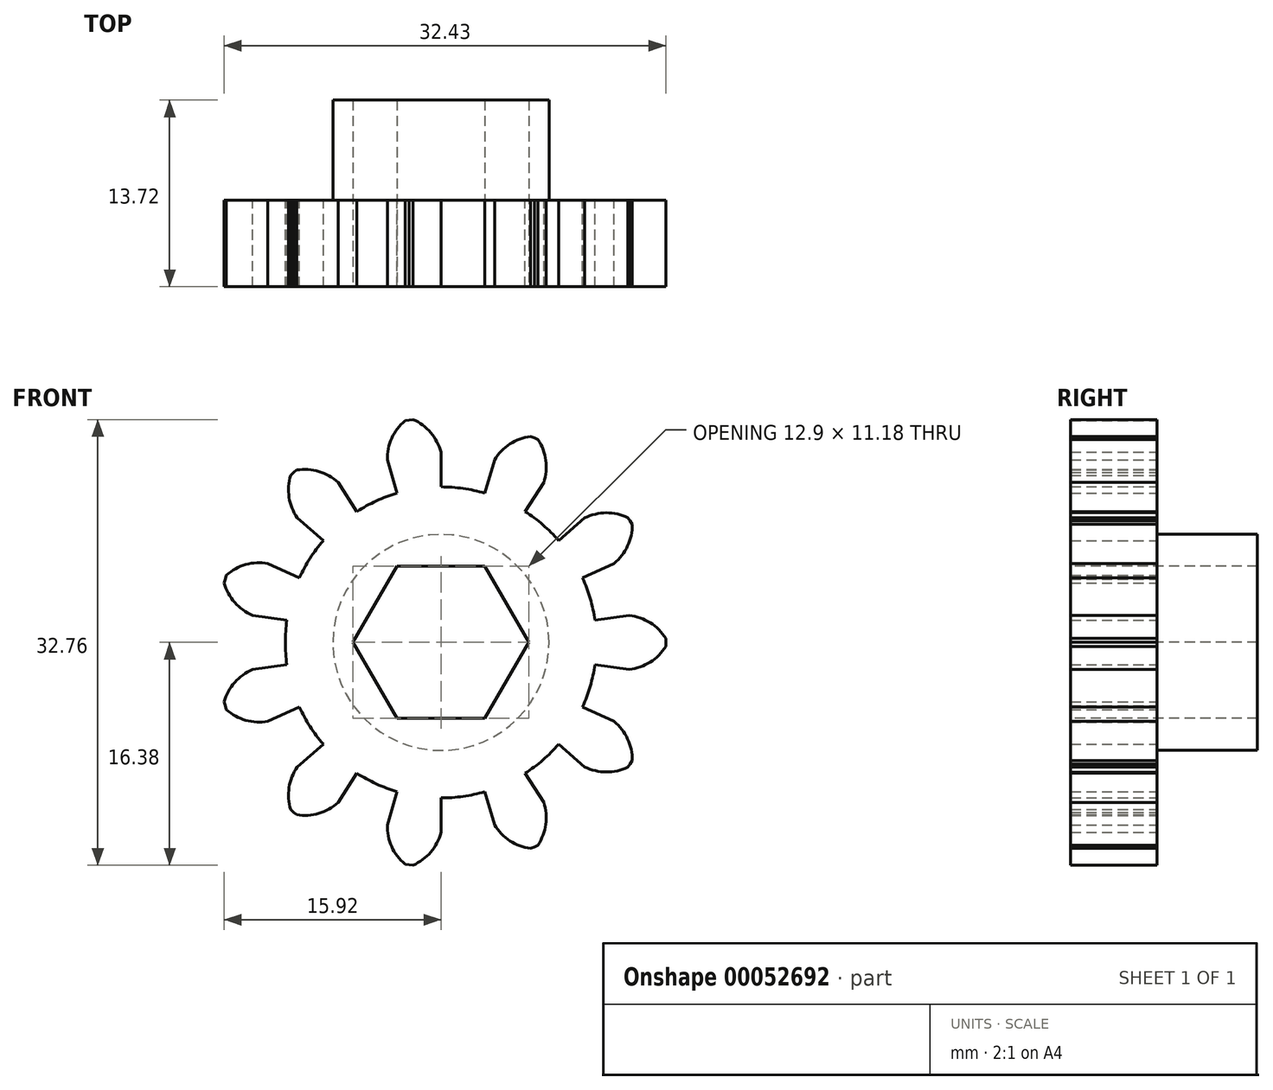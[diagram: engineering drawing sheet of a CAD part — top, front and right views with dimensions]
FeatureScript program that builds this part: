
annotation { "Feature Type Name" : "Feature", "Feature Type Description" : "" }
export const myFeature = defineFeature(function(context is Context, id is Id, definition is map)
    precondition{}
    {
        {
            var Q0;
            Q0=qCreatedBy(makeId("Front.planeOp"),FACE);
            var sketch = newSketch(context, id + "F0", { "sketchPlane" : qUnion([Q0])});
            skArc(sketch, "E0", {"start": v(-3.22, 10.97) * mm, "mid": v(-4.75, 10.4) * mm, "end": v(-6.18, 9.62) * mm});
            skArc(sketch, "E1", {"start": v(0, 13.97) * mm, "mid": v(-0.75, 15.41) * mm, "end": v(-2.06, 16.38) * mm});
            skLineSegment(sketch, "E2", {"start": v(0, 11.43) * mm, "end": v(0, 13.97) * mm});
            skLineSegment(sketch, "E3", {"start": v(-2.06, 16.38) * mm, "end": v(-2.35, 16.34) * mm});
            skLineSegment(sketch, "E4.MirrorCS", {"start": v(-2.64, 16.3) * mm, "end": v(-2.35, 16.34) * mm});
            skArc(sketch, "E5.MirrorCS", {"start": v(-3.93, 13.4) * mm, "mid": v(-3.62, 15) * mm, "end": v(-2.64, 16.3) * mm});
            skLineSegment(sketch, "E6.MirrorCS", {"start": v(-3.22, 10.97) * mm, "end": v(-3.93, 13.4) * mm});
            skLineSegment(sketch, "E7.1.0", {"start": v(-6.18, 9.62) * mm, "end": v(-7.55, 11.75) * mm});
            skArc(sketch, "E7.1.1", {"start": v(-7.55, 11.75) * mm, "mid": v(-8.96, 12.56) * mm, "end": v(-10.59, 12.67) * mm});
            skArc(sketch, "E7.1.2", {"start": v(-10.56, 9.15) * mm, "mid": v(-11.16, 10.66) * mm, "end": v(-11.03, 12.28) * mm});
            skLineSegment(sketch, "E7.1.3", {"start": v(-8.64, 7.49) * mm, "end": v(-10.56, 9.15) * mm});
            skLineSegment(sketch, "E7.1.4", {"start": v(-10.59, 12.67) * mm, "end": v(-10.81, 12.48) * mm});
            skLineSegment(sketch, "E7.1.5", {"start": v(-11.03, 12.28) * mm, "end": v(-10.81, 12.48) * mm});
            skLineSegment(sketch, "E7.2.0", {"start": v(-10.4, 4.75) * mm, "end": v(-12.7, 5.8) * mm});
            skArc(sketch, "E7.2.1", {"start": v(-12.7, 5.8) * mm, "mid": v(-14.33, 5.72) * mm, "end": v(-15.76, 4.93) * mm});
            skArc(sketch, "E7.2.2", {"start": v(-13.83, 1.99) * mm, "mid": v(-15.15, 2.94) * mm, "end": v(-15.92, 4.37) * mm});
            skLineSegment(sketch, "E7.2.3", {"start": v(-11.31, 1.63) * mm, "end": v(-13.83, 1.99) * mm});
            skLineSegment(sketch, "E7.2.4", {"start": v(-15.76, 4.93) * mm, "end": v(-15.84, 4.65) * mm});
            skLineSegment(sketch, "E7.2.5", {"start": v(-15.92, 4.37) * mm, "end": v(-15.84, 4.65) * mm});
            skLineSegment(sketch, "E7.3.0", {"start": v(-11.31, -1.63) * mm, "end": v(-13.83, -1.99) * mm});
            skArc(sketch, "E7.3.1", {"start": v(-13.83, -1.99) * mm, "mid": v(-15.15, -2.94) * mm, "end": v(-15.92, -4.37) * mm});
            skArc(sketch, "E7.3.2", {"start": v(-12.7, -5.8) * mm, "mid": v(-14.33, -5.72) * mm, "end": v(-15.76, -4.93) * mm});
            skLineSegment(sketch, "E7.3.3", {"start": v(-10.4, -4.75) * mm, "end": v(-12.7, -5.8) * mm});
            skLineSegment(sketch, "E7.3.4", {"start": v(-15.92, -4.37) * mm, "end": v(-15.84, -4.65) * mm});
            skLineSegment(sketch, "E7.3.5", {"start": v(-15.76, -4.93) * mm, "end": v(-15.84, -4.65) * mm});
            skLineSegment(sketch, "E7.4.0", {"start": v(-8.64, -7.49) * mm, "end": v(-10.56, -9.15) * mm});
            skArc(sketch, "E7.4.1", {"start": v(-10.56, -9.15) * mm, "mid": v(-11.16, -10.66) * mm, "end": v(-11.03, -12.28) * mm});
            skArc(sketch, "E7.4.2", {"start": v(-7.55, -11.75) * mm, "mid": v(-8.97, -12.56) * mm, "end": v(-10.59, -12.67) * mm});
            skLineSegment(sketch, "E7.4.3", {"start": v(-6.18, -9.62) * mm, "end": v(-7.55, -11.75) * mm});
            skLineSegment(sketch, "E7.4.4", {"start": v(-11.03, -12.28) * mm, "end": v(-10.81, -12.48) * mm});
            skLineSegment(sketch, "E7.4.5", {"start": v(-10.59, -12.67) * mm, "end": v(-10.81, -12.48) * mm});
            skLineSegment(sketch, "E7.5.0", {"start": v(-3.22, -10.97) * mm, "end": v(-3.94, -13.4) * mm});
            skArc(sketch, "E7.5.1", {"start": v(-3.94, -13.4) * mm, "mid": v(-3.62, -15) * mm, "end": v(-2.64, -16.3) * mm});
            skArc(sketch, "E7.5.2", {"start": v(0, -13.97) * mm, "mid": v(-0.75, -15.41) * mm, "end": v(-2.06, -16.38) * mm});
            skLineSegment(sketch, "E7.5.3", {"start": v(0, -11.43) * mm, "end": v(0, -13.97) * mm});
            skLineSegment(sketch, "E7.5.4", {"start": v(-2.64, -16.3) * mm, "end": v(-2.35, -16.34) * mm});
            skLineSegment(sketch, "E7.5.5", {"start": v(-2.06, -16.38) * mm, "end": v(-2.35, -16.34) * mm});
            skLineSegment(sketch, "E7.6.0", {"start": v(3.22, -10.97) * mm, "end": v(3.94, -13.4) * mm});
            skArc(sketch, "E7.6.1", {"start": v(3.94, -13.4) * mm, "mid": v(5.06, -14.58) * mm, "end": v(6.59, -15.14) * mm});
            skArc(sketch, "E7.6.2", {"start": v(7.55, -11.75) * mm, "mid": v(7.7, -13.37) * mm, "end": v(7.12, -14.9) * mm});
            skLineSegment(sketch, "E7.6.3", {"start": v(6.18, -9.62) * mm, "end": v(7.55, -11.75) * mm});
            skLineSegment(sketch, "E7.6.4", {"start": v(6.59, -15.14) * mm, "end": v(6.86, -15.02) * mm});
            skLineSegment(sketch, "E7.6.5", {"start": v(7.12, -14.9) * mm, "end": v(6.86, -15.02) * mm});
            skLineSegment(sketch, "E7.7.0", {"start": v(8.64, -7.49) * mm, "end": v(10.56, -9.15) * mm});
            skArc(sketch, "E7.7.1", {"start": v(10.56, -9.15) * mm, "mid": v(12.14, -9.53) * mm, "end": v(13.73, -9.17) * mm});
            skArc(sketch, "E7.7.2", {"start": v(12.7, -5.8) * mm, "mid": v(13.7, -7.09) * mm, "end": v(14.05, -8.68) * mm});
            skLineSegment(sketch, "E7.7.3", {"start": v(10.4, -4.75) * mm, "end": v(12.7, -5.8) * mm});
            skLineSegment(sketch, "E7.7.4", {"start": v(13.73, -9.17) * mm, "end": v(13.9, -8.93) * mm});
            skLineSegment(sketch, "E7.7.5", {"start": v(14.05, -8.68) * mm, "end": v(13.9, -8.93) * mm});
            skLineSegment(sketch, "E7.8.0", {"start": v(11.31, -1.63) * mm, "end": v(13.83, -1.99) * mm});
            skArc(sketch, "E7.8.1", {"start": v(13.83, -1.99) * mm, "mid": v(15.36, -1.45) * mm, "end": v(16.5, -0.3) * mm});
            skArc(sketch, "E7.8.2", {"start": v(13.83, 1.99) * mm, "mid": v(15.36, 1.45) * mm, "end": v(16.5, 0.3) * mm});
            skLineSegment(sketch, "E7.8.3", {"start": v(11.31, 1.63) * mm, "end": v(13.83, 1.99) * mm});
            skLineSegment(sketch, "E7.8.4", {"start": v(16.5, -0.3) * mm, "end": v(16.51, 0) * mm});
            skLineSegment(sketch, "E7.8.5", {"start": v(16.5, 0.3) * mm, "end": v(16.51, 0) * mm});
            skLineSegment(sketch, "E7.9.0", {"start": v(10.4, 4.75) * mm, "end": v(12.7, 5.8) * mm});
            skArc(sketch, "E7.9.1", {"start": v(12.7, 5.8) * mm, "mid": v(13.7, 7.09) * mm, "end": v(14.05, 8.68) * mm});
            skArc(sketch, "E7.9.2", {"start": v(10.56, 9.15) * mm, "mid": v(12.14, 9.53) * mm, "end": v(13.73, 9.17) * mm});
            skLineSegment(sketch, "E7.9.3", {"start": v(8.64, 7.48) * mm, "end": v(10.56, 9.15) * mm});
            skLineSegment(sketch, "E7.9.4", {"start": v(14.05, 8.68) * mm, "end": v(13.9, 8.93) * mm});
            skLineSegment(sketch, "E7.9.5", {"start": v(13.73, 9.17) * mm, "end": v(13.9, 8.93) * mm});
            skLineSegment(sketch, "E7.10.0", {"start": v(6.18, 9.62) * mm, "end": v(7.55, 11.75) * mm});
            skArc(sketch, "E7.10.1", {"start": v(7.55, 11.75) * mm, "mid": v(7.7, 13.37) * mm, "end": v(7.13, 14.9) * mm});
            skArc(sketch, "E7.10.2", {"start": v(3.94, 13.4) * mm, "mid": v(5.06, 14.58) * mm, "end": v(6.6, 15.14) * mm});
            skLineSegment(sketch, "E7.10.3", {"start": v(3.22, 10.97) * mm, "end": v(3.94, 13.4) * mm});
            skLineSegment(sketch, "E7.10.4", {"start": v(7.13, 14.9) * mm, "end": v(6.86, 15.02) * mm});
            skLineSegment(sketch, "E7.10.5", {"start": v(6.6, 15.14) * mm, "end": v(6.86, 15.02) * mm});
            skArc(sketch, "E8.trimOffspring", {"start": v(-8.64, 7.49) * mm, "mid": v(-9.62, 6.18) * mm, "end": v(-10.4, 4.75) * mm});
            skArc(sketch, "E9.trimOffspring", {"start": v(-11.31, 1.63) * mm, "mid": v(-11.43, 0) * mm, "end": v(-11.31, -1.63) * mm});
            skArc(sketch, "E10.trimOffspring", {"start": v(-10.4, -4.75) * mm, "mid": v(-9.62, -6.18) * mm, "end": v(-8.64, -7.49) * mm});
            skArc(sketch, "E11.trimOffspring", {"start": v(-6.18, -9.62) * mm, "mid": v(-4.75, -10.4) * mm, "end": v(-3.22, -10.97) * mm});
            skArc(sketch, "E12.trimOffspring", {"start": v(0, -11.43) * mm, "mid": v(1.63, -11.31) * mm, "end": v(3.22, -10.97) * mm});
            skArc(sketch, "E13.trimOffspring", {"start": v(6.18, -9.62) * mm, "mid": v(7.48, -8.64) * mm, "end": v(8.64, -7.49) * mm});
            skArc(sketch, "E14.trimOffspring", {"start": v(10.4, -4.75) * mm, "mid": v(10.97, -3.22) * mm, "end": v(11.31, -1.63) * mm});
            skArc(sketch, "E15.trimOffspring", {"start": v(11.31, 1.63) * mm, "mid": v(10.97, 3.22) * mm, "end": v(10.4, 4.75) * mm});
            skArc(sketch, "E16.trimOffspring", {"start": v(8.64, 7.48) * mm, "mid": v(7.49, 8.64) * mm, "end": v(6.18, 9.62) * mm});
            skArc(sketch, "E17.trimOffspring", {"start": v(3.22, 10.97) * mm, "mid": v(1.63, 11.31) * mm, "end": v(0, 11.43) * mm});
            skSolve(sketch);
        }
        {
            var Q0;
            Q0=makeQuery(id+"F0.imprint","IMPRINT",FACE,{"disambiguationData":[TD([[makeQuery(id+"F0.imprint","IMPRINT",EDGE,{"derivedFrom":sQuery(id+"F0.wireOp",EDGE,"E0")}),1.0]])]});
            extrude(context, id + "F1", {"entities" : qUnion([Q0]), "depth" : 6.35 * mm});
        }
        {
            var Q0;
            Q0=qCreatedBy(makeId("Front.planeOp"),FACE);
            var sketch = newSketch(context, id + "F2", { "sketchPlane" : qUnion([Q0])});
            skCircle(sketch, "E18", {"center": v(0, 0) * mm, "radius": 7.94 * mm});
            skSolve(sketch);
        }
        {
            var Q0;
            Q0=makeQuery(id+"F2.imprint","IMPRINT",FACE,{"disambiguationData":[TD([[makeQuery(id+"F2.imprint","IMPRINT",EDGE,{"derivedFrom":sQuery(id+"F2.wireOp",EDGE,"E18")}),1.0]])]});
            extrude(context, id + "F3", {"entities" : qUnion([Q0]), "operationType" : NewBodyOperationType.ADD, "oppositeDirection" : true, "depth" : 7.37 * mm});
        }
        {
            var Q0;
            Q0=qCreatedBy(makeId("Front.planeOp"),FACE);
            var sketch = newSketch(context, id + "F4", { "sketchPlane" : qUnion([Q0])});
            skCircle(sketch, "E19.cCircle", {"center": v(0, 0) * mm, "radius": 6.45 * mm, "construction": true});
            skLineSegment(sketch, "E19.0", {"start": v(6.45, 0) * mm, "end": v(3.23, -5.59) * mm});
            skLineSegment(sketch, "E19.1", {"start": v(3.23, -5.59) * mm, "end": v(-3.23, -5.59) * mm});
            skLineSegment(sketch, "E19.2", {"start": v(-3.23, -5.59) * mm, "end": v(-6.45, 0) * mm});
            skLineSegment(sketch, "E19.3", {"start": v(-6.45, 0) * mm, "end": v(-3.23, 5.59) * mm});
            skLineSegment(sketch, "E19.4", {"start": v(-3.23, 5.59) * mm, "end": v(3.23, 5.59) * mm});
            skLineSegment(sketch, "E19.5", {"start": v(3.23, 5.59) * mm, "end": v(6.45, 0) * mm});
            skSolve(sketch);
        }
        {
            var Q0;
            Q0 = qSketchRegion(id + "F4", true);
            extrude(context, id + "F5", {"entities" : qUnion([Q0]), "operationType" : NewBodyOperationType.REMOVE, "oppositeDirection" : true, "depth" : 25.4 * mm});
        }
        {
            var Q0;
            Q0=makeQuery(id+"F5.boolean.opBoolean","COPY",FACE,{"derivedFrom":makeQuery(id+"F5.opExtrude","CAP_FACE",FACE,{"disambiguationData":[OSD([sQuery(id+"F4.wireOp",EDGE,"E19.0"),sQuery(id+"F4.wireOp",EDGE,"E19.1"),sQuery(id+"F4.wireOp",EDGE,"E19.2"),sQuery(id+"F4.wireOp",EDGE,"E19.3"),sQuery(id+"F4.wireOp",EDGE,"E19.4"),sQuery(id+"F4.wireOp",EDGE,"E19.5")])],"isStart":true})});
            extrude(context, id + "F6", {"entities" : qUnion([Q0]), "operationType" : NewBodyOperationType.REMOVE, "oppositeDirection" : true, "depth" : 25.4 * mm});
        }
    });
